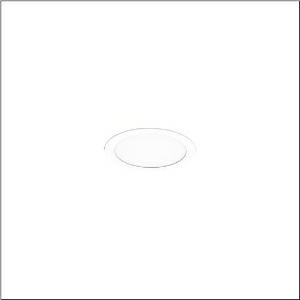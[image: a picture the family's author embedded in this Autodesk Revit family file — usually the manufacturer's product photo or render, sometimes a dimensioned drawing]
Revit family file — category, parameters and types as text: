
# Revit family: lunis_21_m_51db16ec91c
name_source: partatom
category: Lighting Fixtures
units: mm (PartAtom-declared; Revit-internal decimal feet)

## family parameters
Cut with Voids When Loaded = No
Host = Face
Light Source = No
Part Type = Normal
Room Calculation Point = No
Round Connector Dimension = Use Diameter
Shared = No

## types (1)
- --- (1 x LED, 3150 lm, 25.5 W, 6500K)
    Apparent Load = 26 VA
    CIE Flux Codes = 50 80 96 100 100
    Color Rendering = 80
    Color Temperature = 6500K
    Default Elevation = 1800 mm
    Description = Lunis 21,  M, downlight, light control with lens, of PMMA, optical cover: cover panel, of PC, opal, light emission: direct distribution, LED rated luminous flux: 1.460lm, light colour: 830/840/865, with terminal, 5-pole, mains connection: 220..240V, AC/DC, 0/50..60Hz, housing, round, of diecast aluminium, traffic white (RAL 9016), diameter: 115mm, clamping range: 1..40mm, protection rating (complete): IP20, protection rating (on room side): IP54, insulation class (complete): insulation class II (safety insulation), certification: CE, impact resistance: IK03, packaging unit: 1 piece
    Height = 0 mm  [stored 0 ft]
    Lamp = 1 x LED
    Lamp Light Flux = 3150 lm
    Lamp Power = 25.5 W
    Lamp count = 1
    Length = 115 mm
    Luminous efficacy = 124 lm/W
    Manufacturer = Siteco
    ModVariant = No
    Model = 51DB16EC91C
    Mounting Place = Ceiling
    Mounting Type = Recessed
    Number of Poles = 1
    OnlyDefault = Yes
    Power Factor = 1
    Product Name = Lunis 21 M
    Product group = downlight
    ProductGroupID = 400
    Protection Class = Protection class II
    Protection Degree = IP 20
    RLX_Detail_Level = 1
    RLX_Emergency_Light_Flux = 0 lm
    RLX_Emergency_Type = 0
    RLX_Emergency_Type_DB = No
    RlxData = <blob elided: 13453 chars, md5=64d33ef5>
    Socket = socket
    Standby Power = 0 W
    System Light Flux = 3150 lm
    System Power = 26 W
    Type Comments = individual setting: colour temperature 6500K, luminous flux: 100 % | (ON | ON | OFF | OFF) | 700 mA
    Type Image = l_1290848.jpg
    URL = http://relux.com
    VarID = @adj_018430
    Voltage = 0 V
    Weight = 0.00 kg
    Width = 0 mm  [stored 0 ft]

note: [stored X ft] marks values corroborated as IEEE doubles in the binary element streams (Revit-internal decimal feet)

## geometry (parser evidence)
native form markers: Sweep x9
no freeform markers — native parametric forms only
